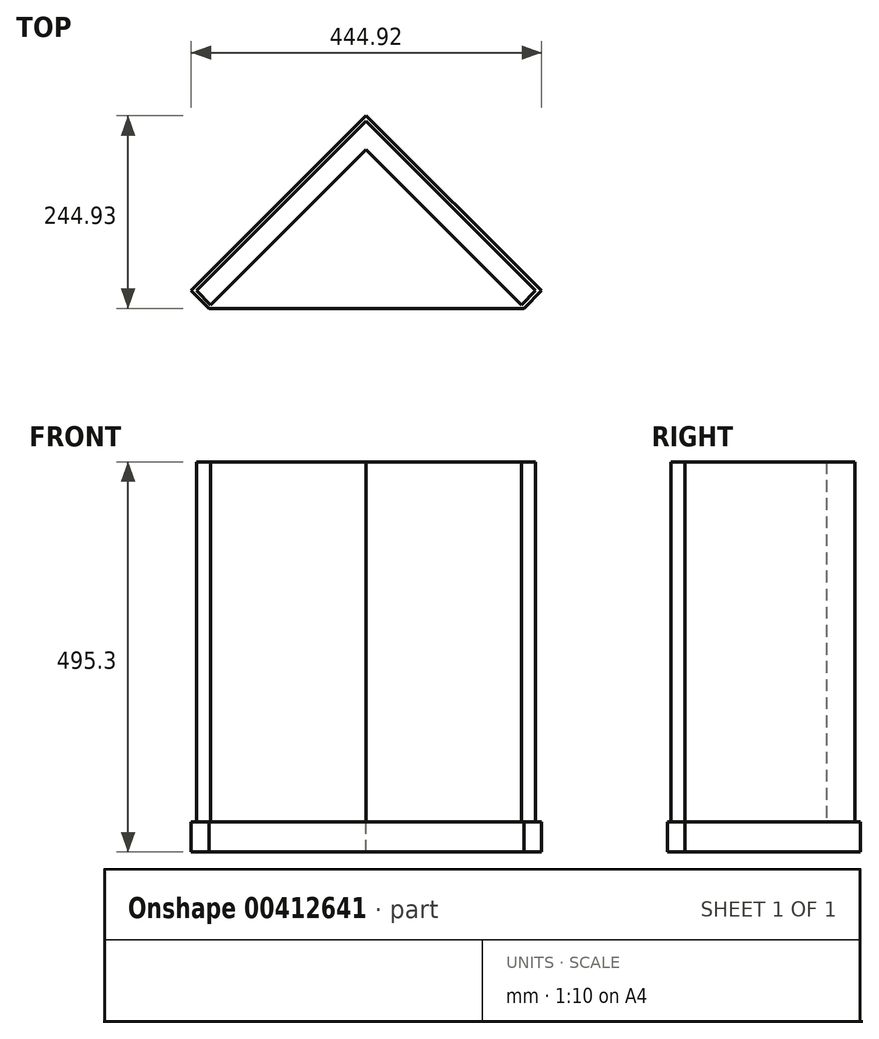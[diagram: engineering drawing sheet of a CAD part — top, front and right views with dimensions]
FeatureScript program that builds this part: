
annotation { "Feature Type Name" : "Feature", "Feature Type Description" : "" }
export const myFeature = defineFeature(function(context is Context, id is Id, definition is map)
    precondition{}
    {
        {
            var Q0;
            Q0=qCreatedBy(makeId("Top.planeOp"),FACE);
            var sketch = newSketch(context, id + "F0", { "sketchPlane" : qUnion([Q0])});
            skLineSegment(sketch, "E0", {"start": v(0, 215.53) * mm, "end": v(-215.53, 0) * mm});
            skLineSegment(sketch, "E1", {"start": v(-215.53, 0) * mm, "end": v(-197.57, -17.96) * mm});
            skLineSegment(sketch, "E2", {"start": v(-197.57, -17.96) * mm, "end": v(0, 179.6) * mm});
            skLineSegment(sketch, "E3", {"start": v(0, 179.6) * mm, "end": v(197.57, -17.96) * mm});
            skLineSegment(sketch, "E4", {"start": v(197.57, -17.96) * mm, "end": v(215.53, 0) * mm});
            skLineSegment(sketch, "E5", {"start": v(215.53, 0) * mm, "end": v(0, 215.53) * mm});
            skSolve(sketch);
        }
        {
            var Q0;
            Q0 = qSketchRegion(id + "F0", true);
            extrude(context, id + "F1", {"entities" : qUnion([Q0]), "depth" : 457.2 * mm});
        }
        {
            var Q0;
            Q0=qCreatedBy(makeId("Top.planeOp"),FACE);
            var sketch = newSketch(context, id + "F2", { "sketchPlane" : qUnion([Q0])});
            skLineSegment(sketch, "E6", {"start": v(-222.07, 0) * mm, "end": v(0, 222.46) * mm});
            skLineSegment(sketch, "E7", {"start": v(0, 222.46) * mm, "end": v(222.85, 0) * mm});
            skLineSegment(sketch, "E8", {"start": v(222.85, 0) * mm, "end": v(200.41, -22.47) * mm});
            skLineSegment(sketch, "E9", {"start": v(200.41, -22.47) * mm, "end": v(-199.64, -22.47) * mm});
            skLineSegment(sketch, "E10", {"start": v(-199.64, -22.47) * mm, "end": v(-222.07, 0) * mm});
            skSolve(sketch);
        }
        {
            var Q0;
            Q0 = qSketchRegion(id + "F2", true);
            var Q1;
            Q1=makeQuery(id+"F1.opExtrude","SWEPT_FACE",FACE,{"disambiguationData":[OSD([sQuery(id+"F0.wireOp",EDGE,"E2")])]});
            extrude(context, id + "F3", {"entities" : qUnion([Q0]), "oppositeDirection" : true, "endBoundEntityFace" : qUnion([Q1]), "depth" : 38.1 * mm});
        }
    });
